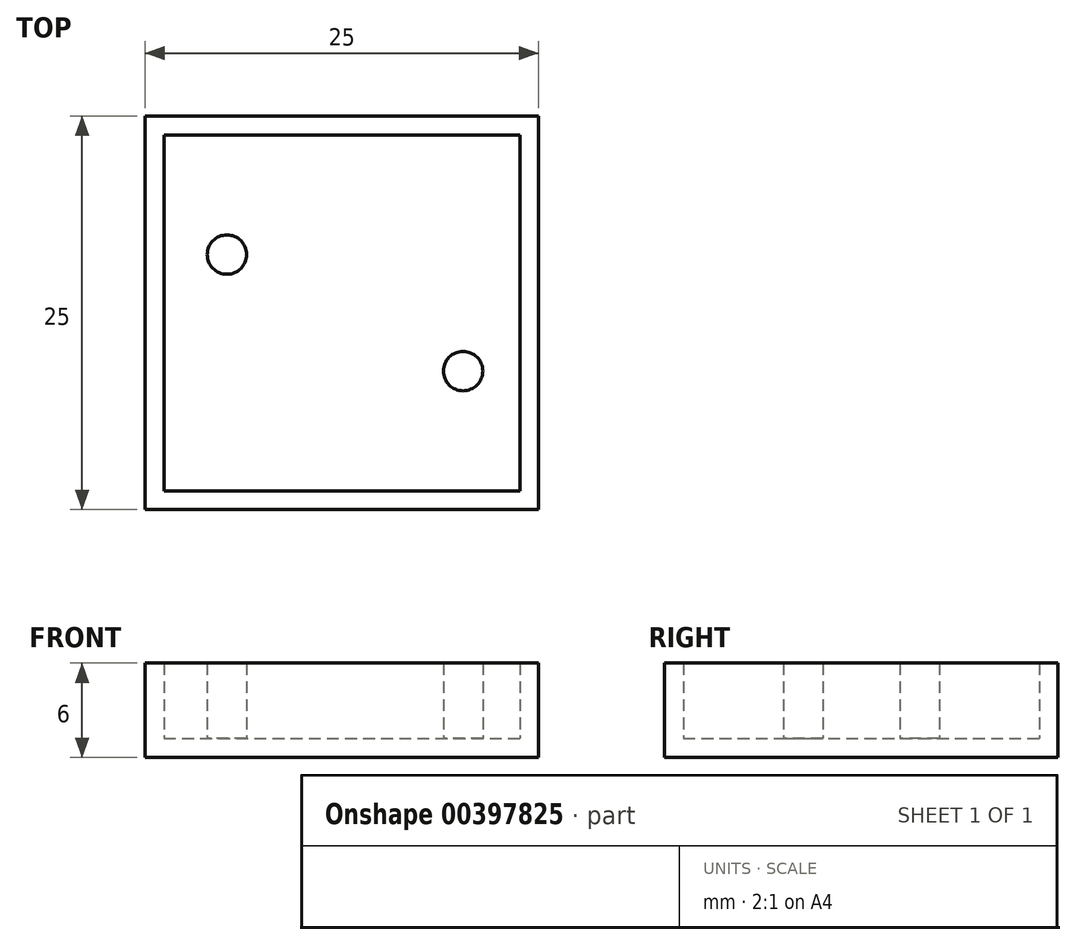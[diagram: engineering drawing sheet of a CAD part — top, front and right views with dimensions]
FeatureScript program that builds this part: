
annotation { "Feature Type Name" : "Feature", "Feature Type Description" : "" }
export const myFeature = defineFeature(function(context is Context, id is Id, definition is map)
    precondition{}
    {
        {
            var Q0;
            Q0=qCreatedBy(makeId("Top.planeOp"),FACE);
            var sketch = newSketch(context, id + "F0", { "sketchPlane" : qUnion([Q0])});
            skLineSegment(sketch, "E0.bottom", {"start": v(-20.1, -18.22) * mm, "end": v(2.5, -18.22) * mm});
            skLineSegment(sketch, "E0.top", {"start": v(-20.1, 4.38) * mm, "end": v(2.5, 4.38) * mm});
            skLineSegment(sketch, "E0.left", {"start": v(-20.1, -18.22) * mm, "end": v(-20.1, 4.38) * mm});
            skLineSegment(sketch, "E0.right", {"start": v(2.5, -18.22) * mm, "end": v(2.5, 4.38) * mm});
            skLineSegment(sketch, "E1.0", {"start": v(-21.3, -19.42) * mm, "end": v(3.7, -19.42) * mm});
            skLineSegment(sketch, "E1.1", {"start": v(-21.3, -19.42) * mm, "end": v(-21.3, 5.58) * mm});
            skLineSegment(sketch, "E1.2", {"start": v(-21.3, 5.58) * mm, "end": v(3.7, 5.58) * mm});
            skLineSegment(sketch, "E1.3", {"start": v(3.7, -19.42) * mm, "end": v(3.7, 5.58) * mm});
            skCircle(sketch, "E2", {"center": v(-16.1, -3.22) * mm, "radius": 1.25 * mm});
            skCircle(sketch, "E3", {"center": v(-1.1, -10.62) * mm, "radius": 1.25 * mm});
            skSolve(sketch);
        }
        {
            var Q0;
            Q0=makeQuery(id+"F0.imprint","IMPRINT",FACE,{"disambiguationData":[TD([[makeQuery(id+"F0.imprint","IMPRINT",EDGE,{"derivedFrom":sQuery(id+"F0.wireOp",EDGE,"E0.bottom")}),1.0]])]});
            extrude(context, id + "F1", {"entities" : qUnion([Q0]), "depth" : 1.2 * mm});
        }
        {
            var Q0;
            Q0=makeQuery(id+"F0.imprint","IMPRINT",FACE,{"disambiguationData":[TD([[makeQuery(id+"F0.imprint","IMPRINT",EDGE,{"derivedFrom":sQuery(id+"F0.wireOp",EDGE,"E0.bottom")}),-1.0]])]});
            var Q1;
            Q1=makeQuery(id+"F0.imprint","IMPRINT",FACE,{"disambiguationData":[TD([[makeQuery(id+"F0.imprint","IMPRINT",EDGE,{"derivedFrom":sQuery(id+"F0.wireOp",EDGE,"E2")}),1.0]])]});
            var Q2;
            Q2=makeQuery(id+"F0.imprint","IMPRINT",FACE,{"disambiguationData":[TD([[makeQuery(id+"F0.imprint","IMPRINT",EDGE,{"derivedFrom":sQuery(id+"F0.wireOp",EDGE,"E3")}),1.0]])]});
            extrude(context, id + "F2", {"entities" : qUnion([Q0, Q1, Q2]), "operationType" : NewBodyOperationType.ADD, "depth" : 6 * mm});
        }
    });
